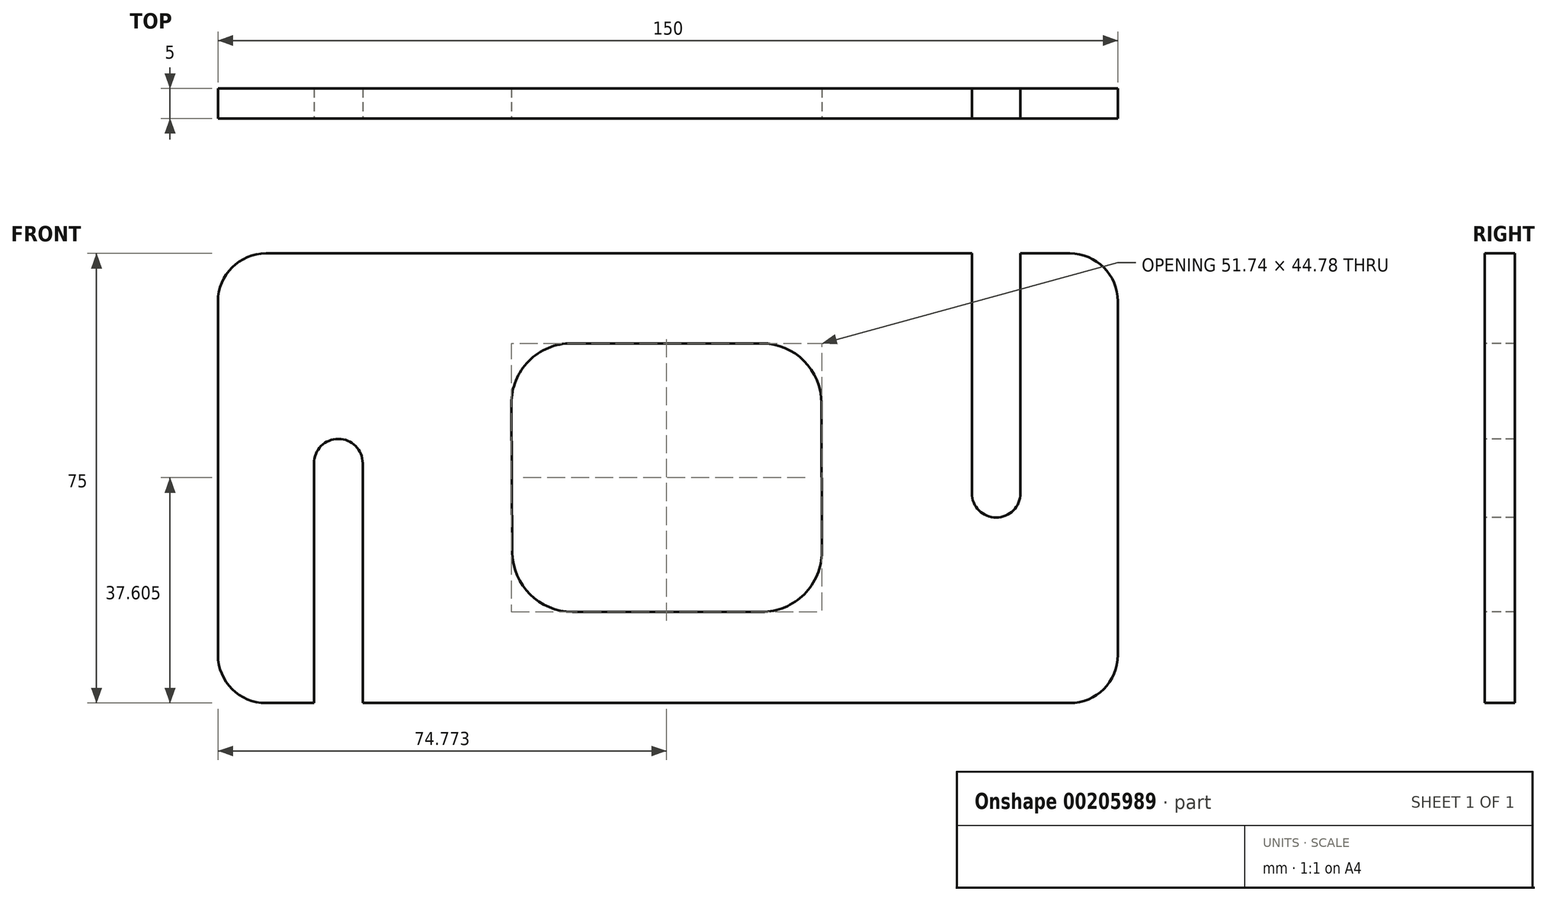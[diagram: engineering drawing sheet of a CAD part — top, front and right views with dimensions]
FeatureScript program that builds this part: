
annotation { "Feature Type Name" : "Feature", "Feature Type Description" : "" }
export const myFeature = defineFeature(function(context is Context, id is Id, definition is map)
    precondition{}
    {
        {
            var Q0;
            Q0=qCreatedBy(makeId("Front.planeOp"),FACE);
            var sketch = newSketch(context, id + "F0", { "sketchPlane" : qUnion([Q0])});
            skLineSegment(sketch, "E0", {"start": v(-75, 28.95) * mm, "end": v(-75, -30.05) * mm});
            skLineSegment(sketch, "E1", {"start": v(-67, -38.05) * mm, "end": v(67, -38.05) * mm});
            skLineSegment(sketch, "E2", {"start": v(75, -30.05) * mm, "end": v(75, 28.95) * mm});
            skLineSegment(sketch, "E3", {"start": v(67, 36.95) * mm, "end": v(-67, 36.95) * mm});
            skPoint(sketch, "E4.visualSharp", {"position": v(-75, 36.95) * mm});
            skArc(sketch, "E4.filletArc", {"start": v(-67, 36.95) * mm, "mid": v(-72.66, 34.6) * mm, "end": v(-75, 28.95) * mm});
            skPoint(sketch, "E5.visualSharp", {"position": v(75, 36.95) * mm});
            skArc(sketch, "E5.filletArc", {"start": v(75, 28.95) * mm, "mid": v(72.66, 34.6) * mm, "end": v(67, 36.95) * mm});
            skPoint(sketch, "E6.visualSharp", {"position": v(75, -38.05) * mm});
            skArc(sketch, "E6.filletArc", {"start": v(67, -38.05) * mm, "mid": v(72.66, -35.71) * mm, "end": v(75, -30.05) * mm});
            skPoint(sketch, "E7.visualSharp", {"position": v(-75, -38.05) * mm});
            skArc(sketch, "E7.filletArc", {"start": v(-75, -30.05) * mm, "mid": v(-72.66, -35.71) * mm, "end": v(-67, -38.05) * mm});
            skSolve(sketch);
        }
        {
            var Q0;
            Q0 = qSketchRegion(id + "F0", true);
            extrude(context, id + "F1", {"entities" : qUnion([Q0]), "depth" : 5 * mm});
        }
        {
            var Q0;
            Q0=makeQuery(id+"F1.opExtrude","CAP_FACE",FACE,{"disambiguationData":[OSD([sQuery(id+"F0.wireOp",EDGE,"E0"),sQuery(id+"F0.wireOp",EDGE,"E1"),sQuery(id+"F0.wireOp",EDGE,"E2"),sQuery(id+"F0.wireOp",EDGE,"E3")])],"isStart":false});
            var sketch = newSketch(context, id + "F2", { "sketchPlane" : qUnion([Q0])});
            skLineSegment(sketch, "E8", {"start": v(-75, -38.05) * mm, "end": v(-59, -38.05) * mm});
            skLineSegment(sketch, "E9", {"start": v(-59, -38.05) * mm, "end": v(-59, 1.95) * mm});
            skArc(sketch, "E10", {"start": v(-59, 1.95) * mm, "mid": v(-54.94, 6) * mm, "end": v(-50.88, 1.95) * mm});
            skLineSegment(sketch, "E11", {"start": v(-50.88, 1.95) * mm, "end": v(-50.88, -38.05) * mm});
            skSolve(sketch);
        }
        {
            var Q0;
            {var subQ0=sQuery(id+"F2.wireOp",EDGE,"E9");Q0=makeQuery(id+"F2.imprint","IMPRINT",FACE,{"disambiguationData":[TD([[makeQuery(id+"F2.imprint","IMPRINT",EDGE,{"derivedFrom":subQ0}),-1.0]])]});}
            var Q1;
            Q1=sQuery(id+"F2.wireOp",EDGE,"E10");
            var Q2;
            Q2=sQuery(id+"F2.wireOp",EDGE,"E9");
            var Q3;
            Q3=sQuery(id+"F2.wireOp",EDGE,"E11");
            extrude(context, id + "F3", {"entities" : qUnion([Q0]), "operationType" : NewBodyOperationType.REMOVE, "surfaceEntities" : qUnion([Q1, Q2, Q3]), "oppositeDirection" : true, "depth" : 25 * mm});
        }
        {
            var Q0;
            Q0=makeQuery(id+"F1.opExtrude","CAP_FACE",FACE,{"disambiguationData":[OSD([sQuery(id+"F0.wireOp",EDGE,"E0"),sQuery(id+"F0.wireOp",EDGE,"E1"),sQuery(id+"F0.wireOp",EDGE,"E2"),sQuery(id+"F0.wireOp",EDGE,"E3")])],"isStart":false});
            var sketch = newSketch(context, id + "F4", { "sketchPlane" : qUnion([Q0])});
            skLineSegment(sketch, "E12", {"start": v(75, -30.05) * mm, "end": v(58.77, 36.95) * mm});
            skLineSegment(sketch, "E13", {"start": v(58.77, 36.95) * mm, "end": v(58.77, -3.05) * mm});
            skLineSegment(sketch, "E14", {"start": v(50.65, -3.05) * mm, "end": v(50.65, 36.95) * mm});
            skArc(sketch, "E15", {"start": v(50.65, -3.05) * mm, "mid": v(54.7, -7.1) * mm, "end": v(58.77, -3.05) * mm});
            skSolve(sketch);
        }
        {
            var Q0;
            Q0 = qSketchRegion(id + "F4", true);
            var Q1;
            {var subQ0=sQuery(id+"F4.wireOp",EDGE,"E13");Q1=makeQuery(id+"F4.imprint","IMPRINT",FACE,{"disambiguationData":[TD([[makeQuery(id+"F4.imprint","IMPRINT",EDGE,{"derivedFrom":subQ0}),-1.0]])]});}
            extrude(context, id + "F5", {"entities" : qUnion([Q0, Q1]), "operationType" : NewBodyOperationType.REMOVE, "oppositeDirection" : true, "depth" : 73 * mm});
        }
        {
            var Q0;
            Q0=makeQuery(id+"F1.opExtrude","CAP_FACE",FACE,{"disambiguationData":[OSD([sQuery(id+"F0.wireOp",EDGE,"E0"),sQuery(id+"F0.wireOp",EDGE,"E1"),sQuery(id+"F0.wireOp",EDGE,"E2"),sQuery(id+"F0.wireOp",EDGE,"E3")])],"isStart":false});
            var sketch = newSketch(context, id + "F6", { "sketchPlane" : qUnion([Q0])});
            skLineSegment(sketch, "E16", {"start": v(15.61, 21.95) * mm, "end": v(-16.1, 21.95) * mm});
            skLineSegment(sketch, "E17", {"start": v(-15.94, -22.84) * mm, "end": v(15.64, -22.84) * mm});
            skLineSegment(sketch, "E18", {"start": v(-26.1, 11.88) * mm, "end": v(-25.94, -12.9) * mm});
            skLineSegment(sketch, "E19", {"start": v(25.61, 11.96) * mm, "end": v(25.64, -12.82) * mm});
            skPoint(sketch, "E20.visualSharp", {"position": v(-26.16, 21.95) * mm});
            skArc(sketch, "E20.filletArc", {"start": v(-16.1, 21.95) * mm, "mid": v(-23.19, 19) * mm, "end": v(-26.1, 11.88) * mm});
            skPoint(sketch, "E21.visualSharp", {"position": v(25.6, 21.95) * mm});
            skArc(sketch, "E21.filletArc", {"start": v(25.61, 11.96) * mm, "mid": v(22.68, 19.02) * mm, "end": v(15.61, 21.95) * mm});
            skPoint(sketch, "E22.visualSharp", {"position": v(25.65, -22.84) * mm});
            skArc(sketch, "E22.filletArc", {"start": v(15.64, -22.84) * mm, "mid": v(22.72, -19.9) * mm, "end": v(25.64, -12.82) * mm});
            skPoint(sketch, "E23.visualSharp", {"position": v(-25.88, -22.84) * mm});
            skArc(sketch, "E23.filletArc", {"start": v(-25.94, -12.9) * mm, "mid": v(-23, -19.93) * mm, "end": v(-15.94, -22.84) * mm});
            skSolve(sketch);
        }
        {
            var Q0;
            Q0=makeQuery(id+"F6.imprint","IMPRINT",FACE,{"disambiguationData":[TD([[makeQuery(id+"F6.imprint","IMPRINT",EDGE,{"derivedFrom":sQuery(id+"F6.wireOp",EDGE,"E16")}),1.0]])]});
            extrude(context, id + "F7", {"entities" : qUnion([Q0]), "operationType" : NewBodyOperationType.REMOVE, "oppositeDirection" : true, "depth" : 25 * mm});
        }
    });
